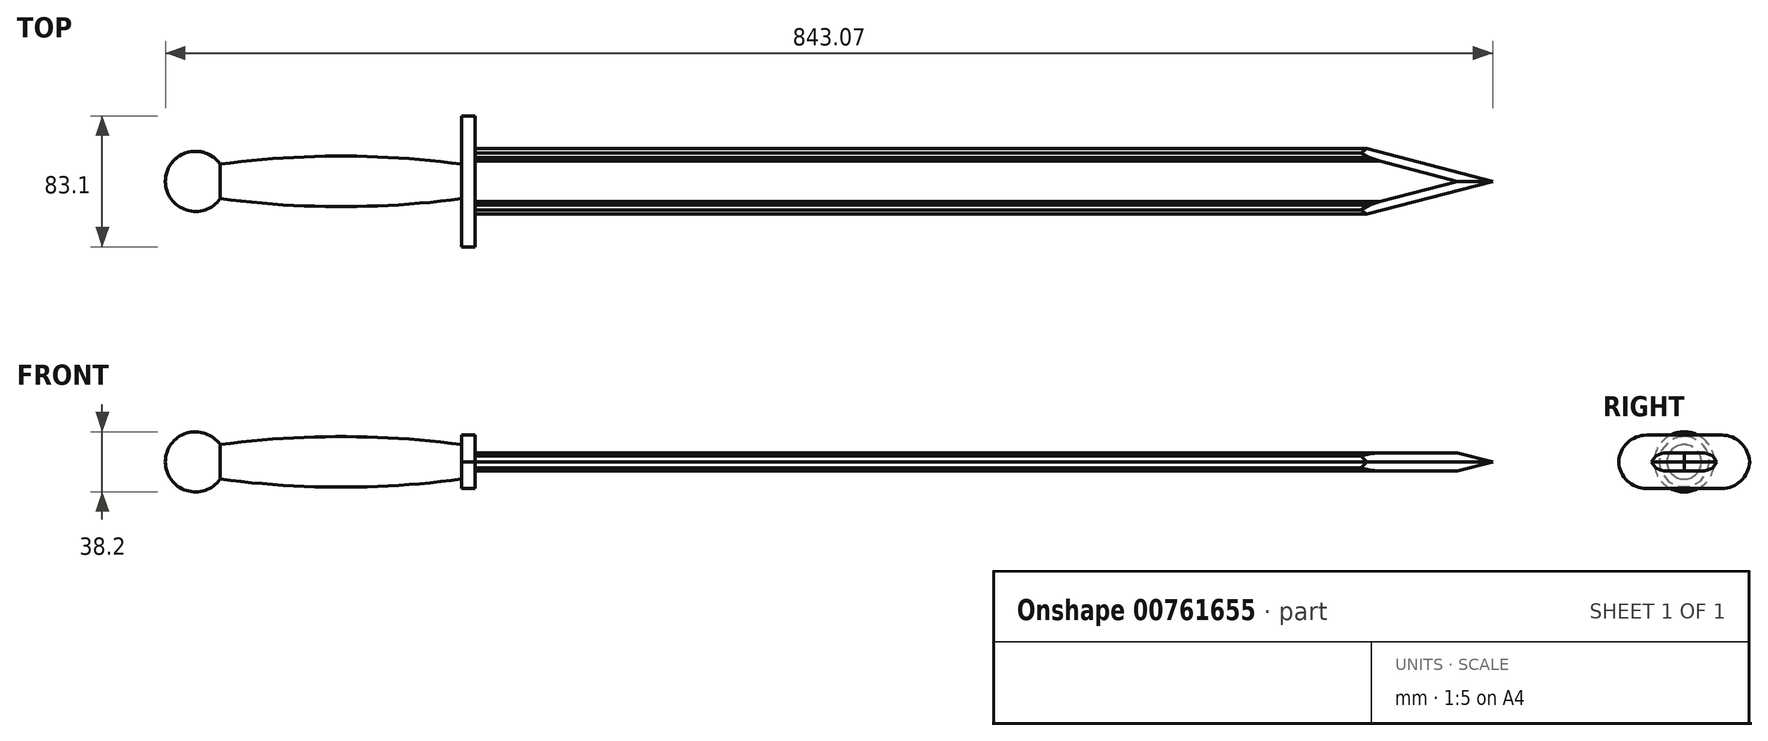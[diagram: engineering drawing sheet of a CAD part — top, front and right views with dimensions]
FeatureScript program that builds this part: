
annotation { "Feature Type Name" : "Feature", "Feature Type Description" : "" }
export const myFeature = defineFeature(function(context is Context, id is Id, definition is map)
    precondition{}
    {
        {
            var Q0;
            Q0=qCreatedBy(makeId("Top.planeOp"),FACE);
            var sketch = newSketch(context, id + "F0", { "sketchPlane" : qUnion([Q0])});
            skLineSegment(sketch, "E0.bottom", {"start": v(-110.92, 0) * mm, "end": v(77.19, 0) * mm});
            skLineSegment(sketch, "E0.right", {"start": v(77.19, 0) * mm, "end": v(77.19, 10.97) * mm});
            skArc(sketch, "E1", {"start": v(-76.16, 10.93) * mm, "mid": v(-97.55, 18.22) * mm, "end": v(-110.92, 0) * mm});
            skArc(sketch, "E2", {"start": v(77.19, 10.97) * mm, "mid": v(0.51, 16.04) * mm, "end": v(-76.16, 10.93) * mm});
            skSolve(sketch);
        }
        {
            var Q0;
            Q0 = qSketchRegion(id + "F0", true);
            var Q1;
            Q1=sQuery(id+"F0.wireOp",EDGE,"E0.bottom");
            revolve(context, id + "F1", {"surfaceOperationType" : NewSurfaceOperationType.NEW, "entities" : qUnion([Q0]), "axis" : qUnion([Q1]), "revolveType" : RevolveType.FULL});
        }
        {
            var Q0;
            Q0=makeQuery(id+"F1.opRevolve","SWEPT_FACE",FACE,{"disambiguationData":[OSD([sQuery(id+"F0.wireOp",EDGE,"E0.right")])]});
            var sketch = newSketch(context, id + "F2", { "sketchPlane" : qUnion([Q0])});
            skLineSegment(sketch, "E3.bottom", {"start": v(-41.57, 17) * mm, "end": v(41.57, 17) * mm});
            skLineSegment(sketch, "E3.top", {"start": v(-41.57, -17) * mm, "end": v(41.57, -17) * mm});
            skLineSegment(sketch, "E3.left", {"start": v(-41.57, 17) * mm, "end": v(-41.57, -17) * mm});
            skLineSegment(sketch, "E3.right", {"start": v(41.57, 17) * mm, "end": v(41.57, -17) * mm});
            skPoint(sketch, "E3.middle", {"position": v(0, 0) * mm});
            skSolve(sketch);
        }
        {
            var Q0;
            Q0 = qSketchRegion(id + "F2", true);
            extrude(context, id + "F3", {"entities" : qUnion([Q0]), "operationType" : NewBodyOperationType.ADD, "depth" : 8.64 * mm, "offsetDistance" : 25.4 * mm});
        }
        {
            var Q0;
            Q0=makeQuery(id+"F3.opExtrude","SWEPT_EDGE",EDGE,{"disambiguationData":[OSD([sQuery(id+"F2.wireOp",EDGE,"E3.bottom"),sQuery(id+"F2.wireOp",EDGE,"E3.right")])]});
            var Q1;
            Q1=makeQuery(id+"F3.opExtrude","SWEPT_EDGE",EDGE,{"disambiguationData":[OSD([sQuery(id+"F2.wireOp",EDGE,"E3.bottom"),sQuery(id+"F2.wireOp",EDGE,"E3.left")])]});
            var Q2;
            Q2=makeQuery(id+"F3.opExtrude","SWEPT_EDGE",EDGE,{"disambiguationData":[OSD([sQuery(id+"F2.wireOp",EDGE,"E3.top"),sQuery(id+"F2.wireOp",EDGE,"E3.left")])]});
            var Q3;
            Q3=makeQuery(id+"F3.opExtrude","SWEPT_EDGE",EDGE,{"disambiguationData":[OSD([sQuery(id+"F2.wireOp",EDGE,"E3.top"),sQuery(id+"F2.wireOp",EDGE,"E3.right")])]});
            fillet(context, id + "F4", {"entities" : qUnion([Q0, Q1, Q2, Q3]), "radius" : 17.78 * mm, "tangentPropagation" : true, "allowEdgeOverflow" : false});
        }
        {
            var Q0;
            Q0=makeQuery(id+"F3.opExtrude","CAP_FACE",FACE,{"disambiguationData":[OSD([sQuery(id+"F2.wireOp",EDGE,"E3.bottom"),sQuery(id+"F2.wireOp",EDGE,"E3.top"),sQuery(id+"F2.wireOp",EDGE,"E3.left"),sQuery(id+"F2.wireOp",EDGE,"E3.right")])],"isStart":false});
            var sketch = newSketch(context, id + "F5", { "sketchPlane" : qUnion([Q0])});
            skLineSegment(sketch, "E4.bottom", {"start": v(22.3, 5.66) * mm, "end": v(-22.3, 5.66) * mm});
            skLineSegment(sketch, "E4.top", {"start": v(22.3, -5.66) * mm, "end": v(-22.3, -5.66) * mm});
            skLineSegment(sketch, "E4.left", {"start": v(22.3, 5.66) * mm, "end": v(22.3, -5.66) * mm});
            skLineSegment(sketch, "E4.right", {"start": v(-22.3, 5.66) * mm, "end": v(-22.3, -5.66) * mm});
            skPoint(sketch, "E4.middle", {"position": v(0, 0) * mm});
            skSolve(sketch);
        }
        {
            var Q0;
            Q0=makeQuery(id+"F5.imprint","IMPRINT",FACE,{"disambiguationData":[TD([[makeQuery(id+"F5.imprint","IMPRINT",EDGE,{"derivedFrom":sQuery(id+"F5.wireOp",EDGE,"E4.bottom")}),1.0]])]});
            extrude(context, id + "F6", {"entities" : qUnion([Q0]), "depth" : 14.48 * mm, "offsetDistance" : 25.4 * mm});
        }
        {
            var Q0;
            Q0=makeQuery(id+"F6.opExtrude","SWEPT_FACE",FACE,{"disambiguationData":[OSD([sQuery(id+"F5.wireOp",EDGE,"E4.bottom")])]});
            var sketch = newSketch(context, id + "F7", { "sketchPlane" : qUnion([Q0])});
            skLineSegment(sketch, "E5.bottom", {"start": v(85.82, 22.3) * mm, "end": v(646.83, 22.3) * mm});
            skLineSegment(sketch, "E5.top", {"start": v(85.82, -22.3) * mm, "end": v(646.83, -22.3) * mm});
            skLineSegment(sketch, "E5.left", {"start": v(85.82, 22.3) * mm, "end": v(85.82, -22.3) * mm});
            skLineSegment(sketch, "E6", {"start": v(732.15, 0) * mm, "end": v(646.83, -22.3) * mm});
            skLineSegment(sketch, "E7", {"start": v(732.15, 0) * mm, "end": v(646.83, 22.3) * mm});
            skSolve(sketch);
        }
        {
            var Q0;
            {var subQ3=sQuery(id+"F7.wireOp",EDGE,"E6");Q0=makeQuery(id+"F7.imprint","IMPRINT",FACE,{"disambiguationData":[TD([[makeQuery(id+"F7.imprint","IMPRINT",EDGE,{"derivedFrom":subQ3}),-1.0]])]});}
            extrude(context, id + "F8", {"entities" : qUnion([Q0]), "oppositeDirection" : true, "depth" : 11.43 * mm, "offsetDistance" : 25.4 * mm});
        }
        {
            var Q0;
            Q0=makeQuery(id+"F8.opExtrude","CAP_EDGE",EDGE,{"disambiguationData":[OSD([sQuery(id+"F7.wireOp",EDGE,"E5.bottom")])],"isStart":true});
            var Q1;
            Q1=makeQuery(id+"F8.opExtrude","CAP_EDGE",EDGE,{"disambiguationData":[OSD([sQuery(id+"F7.wireOp",EDGE,"E5.top")])],"isStart":true});
            var Q2;
            Q2=makeQuery(id+"F8.opExtrude","CAP_EDGE",EDGE,{"disambiguationData":[OSD([sQuery(id+"F7.wireOp",EDGE,"E5.top")])],"isStart":false});
            var Q3;
            Q3=makeQuery(id+"F8.opExtrude","CAP_EDGE",EDGE,{"disambiguationData":[OSD([sQuery(id+"F7.wireOp",EDGE,"E5.bottom")])],"isStart":false});
            chamfer(context, id + "F9", {"entities" : qUnion([Q0, Q1, Q2, Q3]), "chamferType" : ChamferType.TWO_OFFSETS, "width1" : 7.62 * mm, "oppositeDirection" : false, "width2" : 5.7 * mm, "tangentPropagation" : true});
        }
        {
            var Q0;
            {var subQ0=sQuery(id+"F7.wireOp",EDGE,"E5.bottom");var subQ1=sQuery(id+"F5.wireOp",EDGE,"E4.bottom");Q0=makeQuery(id+"F9.opChamfer","BLEND_EDGE",EDGE,{"blendedFrom":[makeQuery(id+"F8.boolean.opBoolean","MERGE",EDGE,{"derivedFrom":[makeQuery(id+"F6.opExtrude","SWEPT_EDGE",EDGE,{"disambiguationData":[OSD([subQ1,sQuery(id+"F5.wireOp",EDGE,"E4.left")])]}),makeQuery(id+"F8.opExtrude","CAP_EDGE",EDGE,{"disambiguationData":[OSD([subQ0])],"isStart":true})]}),makeQuery(id+"F8.boolean.opBoolean","MERGE",FACE,{"derivedFrom":[makeQuery(id+"F6.opExtrude","SWEPT_FACE",FACE,{"disambiguationData":[OSD([subQ1])]}),makeQuery(id+"F8.opExtrude","CAP_FACE",FACE,{"disambiguationData":[OSD([subQ1,subQ0,sQuery(id+"F7.wireOp",EDGE,"E5.top"),sQuery(id+"F7.wireOp",EDGE,"E6"),sQuery(id+"F7.wireOp",EDGE,"E7")])],"isStart":true})]})],"blendedInto":[makeQuery(id+"F8.boolean.opBoolean","MERGE",FACE,{"derivedFrom":[makeQuery(id+"F6.opExtrude","SWEPT_FACE",FACE,{"disambiguationData":[OSD([subQ1])]}),makeQuery(id+"F8.opExtrude","CAP_FACE",FACE,{"disambiguationData":[OSD([subQ1,subQ0,sQuery(id+"F7.wireOp",EDGE,"E5.top"),sQuery(id+"F7.wireOp",EDGE,"E6"),sQuery(id+"F7.wireOp",EDGE,"E7")])],"isStart":true})]})]});}
            var Q1;
            {var subQ0=sQuery(id+"F7.wireOp",EDGE,"E5.top");var subQ1=sQuery(id+"F5.wireOp",EDGE,"E4.bottom");Q1=makeQuery(id+"F9.opChamfer","BLEND_EDGE",EDGE,{"blendedFrom":[makeQuery(id+"F8.boolean.opBoolean","MERGE",EDGE,{"derivedFrom":[makeQuery(id+"F6.opExtrude","SWEPT_EDGE",EDGE,{"disambiguationData":[OSD([subQ1,sQuery(id+"F5.wireOp",EDGE,"E4.right")])]}),makeQuery(id+"F8.opExtrude","CAP_EDGE",EDGE,{"disambiguationData":[OSD([subQ0])],"isStart":true})]}),makeQuery(id+"F8.boolean.opBoolean","MERGE",FACE,{"derivedFrom":[makeQuery(id+"F6.opExtrude","SWEPT_FACE",FACE,{"disambiguationData":[OSD([subQ1])]}),makeQuery(id+"F8.opExtrude","CAP_FACE",FACE,{"disambiguationData":[OSD([subQ1,sQuery(id+"F7.wireOp",EDGE,"E5.bottom"),subQ0,sQuery(id+"F7.wireOp",EDGE,"E6"),sQuery(id+"F7.wireOp",EDGE,"E7")])],"isStart":true})]})],"blendedInto":[makeQuery(id+"F8.boolean.opBoolean","MERGE",FACE,{"derivedFrom":[makeQuery(id+"F6.opExtrude","SWEPT_FACE",FACE,{"disambiguationData":[OSD([subQ1])]}),makeQuery(id+"F8.opExtrude","CAP_FACE",FACE,{"disambiguationData":[OSD([subQ1,sQuery(id+"F7.wireOp",EDGE,"E5.bottom"),subQ0,sQuery(id+"F7.wireOp",EDGE,"E6"),sQuery(id+"F7.wireOp",EDGE,"E7")])],"isStart":true})]})]});}
            chamfer(context, id + "F10", {"entities" : qUnion([Q0, Q1]), "width" : 5.08 * mm, "tangentPropagation" : true});
        }
        {
            var Q0;
            {var subQ0=sQuery(id+"F7.wireOp",EDGE,"E5.bottom");var subQ1=sQuery(id+"F5.wireOp",EDGE,"E4.bottom");var subQ2=makeQuery(id+"F8.boolean.opBoolean","MERGE",FACE,{"derivedFrom":[makeQuery(id+"F6.opExtrude","SWEPT_FACE",FACE,{"disambiguationData":[OSD([subQ1])]}),makeQuery(id+"F8.opExtrude","CAP_FACE",FACE,{"disambiguationData":[OSD([subQ1,subQ0,sQuery(id+"F7.wireOp",EDGE,"E5.top"),sQuery(id+"F7.wireOp",EDGE,"E6"),sQuery(id+"F7.wireOp",EDGE,"E7")])],"isStart":true})]});Q0=makeQuery(id+"F10.opChamfer","BLEND_EDGE",EDGE,{"blendedFrom":[makeQuery(id+"F9.opChamfer","BLEND_EDGE",EDGE,{"blendedFrom":[makeQuery(id+"F8.boolean.opBoolean","MERGE",EDGE,{"derivedFrom":[makeQuery(id+"F6.opExtrude","SWEPT_EDGE",EDGE,{"disambiguationData":[OSD([subQ1,sQuery(id+"F5.wireOp",EDGE,"E4.left")])]}),makeQuery(id+"F8.opExtrude","CAP_EDGE",EDGE,{"disambiguationData":[OSD([subQ0])],"isStart":true})]}),subQ2],"blendedInto":[subQ2]}),subQ2],"blendedInto":[subQ2]});}
            var Q1;
            {var subQ0=sQuery(id+"F7.wireOp",EDGE,"E5.top");var subQ1=sQuery(id+"F5.wireOp",EDGE,"E4.bottom");var subQ2=makeQuery(id+"F8.boolean.opBoolean","MERGE",FACE,{"derivedFrom":[makeQuery(id+"F6.opExtrude","SWEPT_FACE",FACE,{"disambiguationData":[OSD([subQ1])]}),makeQuery(id+"F8.opExtrude","CAP_FACE",FACE,{"disambiguationData":[OSD([subQ1,sQuery(id+"F7.wireOp",EDGE,"E5.bottom"),subQ0,sQuery(id+"F7.wireOp",EDGE,"E6"),sQuery(id+"F7.wireOp",EDGE,"E7")])],"isStart":true})]});Q1=makeQuery(id+"F10.opChamfer","BLEND_EDGE",EDGE,{"blendedFrom":[makeQuery(id+"F9.opChamfer","BLEND_EDGE",EDGE,{"blendedFrom":[makeQuery(id+"F8.boolean.opBoolean","MERGE",EDGE,{"derivedFrom":[makeQuery(id+"F6.opExtrude","SWEPT_EDGE",EDGE,{"disambiguationData":[OSD([subQ1,sQuery(id+"F5.wireOp",EDGE,"E4.right")])]}),makeQuery(id+"F8.opExtrude","CAP_EDGE",EDGE,{"disambiguationData":[OSD([subQ0])],"isStart":true})]}),subQ2],"blendedInto":[subQ2]}),subQ2],"blendedInto":[subQ2]});}
            chamfer(context, id + "F11", {"entities" : qUnion([Q0, Q1]), "width" : 5.08 * mm, "tangentPropagation" : true});
        }
        {
            var Q0;
            Q0=makeQuery(id+"F8.opExtrude","CAP_EDGE",EDGE,{"disambiguationData":[OSD([sQuery(id+"F7.wireOp",EDGE,"E7")])],"isStart":true});
            var Q1;
            Q1=makeQuery(id+"F8.opExtrude","CAP_EDGE",EDGE,{"disambiguationData":[OSD([sQuery(id+"F7.wireOp",EDGE,"E6")])],"isStart":true});
            chamfer(context, id + "F12", {"entities" : qUnion([Q0, Q1]), "width" : 5.7 * mm, "tangentPropagation" : true});
        }
        {
            var Q0;
            {var subQ0=sQuery(id+"F7.wireOp",EDGE,"E5.bottom");Q0=makeQuery(id+"F9.opChamfer","BLEND_EDGE",EDGE,{"blendedFrom":[makeQuery(id+"F8.opExtrude","CAP_EDGE",EDGE,{"disambiguationData":[OSD([subQ0])],"isStart":false}),makeQuery(id+"F8.opExtrude","CAP_FACE",FACE,{"disambiguationData":[OSD([sQuery(id+"F5.wireOp",EDGE,"E4.bottom"),subQ0,sQuery(id+"F7.wireOp",EDGE,"E5.top"),sQuery(id+"F7.wireOp",EDGE,"E6"),sQuery(id+"F7.wireOp",EDGE,"E7")])],"isStart":false})],"blendedInto":[makeQuery(id+"F8.opExtrude","CAP_FACE",FACE,{"disambiguationData":[OSD([sQuery(id+"F5.wireOp",EDGE,"E4.bottom"),subQ0,sQuery(id+"F7.wireOp",EDGE,"E5.top"),sQuery(id+"F7.wireOp",EDGE,"E6"),sQuery(id+"F7.wireOp",EDGE,"E7")])],"isStart":false})]});}
            var Q1;
            {var subQ0=sQuery(id+"F7.wireOp",EDGE,"E5.top");Q1=makeQuery(id+"F9.opChamfer","BLEND_EDGE",EDGE,{"blendedFrom":[makeQuery(id+"F8.opExtrude","CAP_EDGE",EDGE,{"disambiguationData":[OSD([subQ0])],"isStart":false}),makeQuery(id+"F8.opExtrude","CAP_FACE",FACE,{"disambiguationData":[OSD([sQuery(id+"F5.wireOp",EDGE,"E4.bottom"),sQuery(id+"F7.wireOp",EDGE,"E5.bottom"),subQ0,sQuery(id+"F7.wireOp",EDGE,"E6"),sQuery(id+"F7.wireOp",EDGE,"E7")])],"isStart":false})],"blendedInto":[makeQuery(id+"F8.opExtrude","CAP_FACE",FACE,{"disambiguationData":[OSD([sQuery(id+"F5.wireOp",EDGE,"E4.bottom"),sQuery(id+"F7.wireOp",EDGE,"E5.bottom"),subQ0,sQuery(id+"F7.wireOp",EDGE,"E6"),sQuery(id+"F7.wireOp",EDGE,"E7")])],"isStart":false})]});}
            chamfer(context, id + "F13", {"entities" : qUnion([Q0, Q1]), "width" : 5.08 * mm, "tangentPropagation" : true});
        }
        {
            var Q0;
            {var subQ0=sQuery(id+"F7.wireOp",EDGE,"E5.bottom");var subQ1=makeQuery(id+"F8.opExtrude","CAP_FACE",FACE,{"disambiguationData":[OSD([sQuery(id+"F5.wireOp",EDGE,"E4.bottom"),subQ0,sQuery(id+"F7.wireOp",EDGE,"E5.top"),sQuery(id+"F7.wireOp",EDGE,"E6"),sQuery(id+"F7.wireOp",EDGE,"E7")])],"isStart":false});Q0=makeQuery(id+"F13.opChamfer","BLEND_EDGE",EDGE,{"blendedFrom":[makeQuery(id+"F9.opChamfer","BLEND_EDGE",EDGE,{"blendedFrom":[makeQuery(id+"F8.opExtrude","CAP_EDGE",EDGE,{"disambiguationData":[OSD([subQ0])],"isStart":false}),subQ1],"blendedInto":[subQ1]}),subQ1],"blendedInto":[subQ1]});}
            var Q1;
            {var subQ0=sQuery(id+"F7.wireOp",EDGE,"E5.top");var subQ1=makeQuery(id+"F8.opExtrude","CAP_FACE",FACE,{"disambiguationData":[OSD([sQuery(id+"F5.wireOp",EDGE,"E4.bottom"),sQuery(id+"F7.wireOp",EDGE,"E5.bottom"),subQ0,sQuery(id+"F7.wireOp",EDGE,"E6"),sQuery(id+"F7.wireOp",EDGE,"E7")])],"isStart":false});Q1=makeQuery(id+"F13.opChamfer","BLEND_EDGE",EDGE,{"blendedFrom":[makeQuery(id+"F9.opChamfer","BLEND_EDGE",EDGE,{"blendedFrom":[makeQuery(id+"F8.opExtrude","CAP_EDGE",EDGE,{"disambiguationData":[OSD([subQ0])],"isStart":false}),subQ1],"blendedInto":[subQ1]}),subQ1],"blendedInto":[subQ1]});}
            chamfer(context, id + "F14", {"entities" : qUnion([Q0, Q1]), "width" : 5.08 * mm, "tangentPropagation" : true});
        }
        {
            var Q0;
            Q0=makeQuery(id+"F8.opExtrude","CAP_EDGE",EDGE,{"disambiguationData":[OSD([sQuery(id+"F7.wireOp",EDGE,"E7")])],"isStart":false});
            var Q1;
            Q1=makeQuery(id+"F8.opExtrude","CAP_EDGE",EDGE,{"disambiguationData":[OSD([sQuery(id+"F7.wireOp",EDGE,"E6")])],"isStart":false});
            chamfer(context, id + "F15", {"entities" : qUnion([Q0, Q1]), "width" : 5.7 * mm, "tangentPropagation" : true});
        }
        {
            var Q0;
            Q0=makeQuery(id+"F6.opExtrude","SWEPT_EDGE",EDGE,{"disambiguationData":[OSD([sQuery(id+"F5.wireOp",EDGE,"E4.top"),sQuery(id+"F5.wireOp",EDGE,"E4.left")])]});
            var Q1;
            Q1=makeQuery(id+"F6.opExtrude","SWEPT_EDGE",EDGE,{"disambiguationData":[OSD([sQuery(id+"F5.wireOp",EDGE,"E4.top"),sQuery(id+"F5.wireOp",EDGE,"E4.right")])]});
            var Q2;
            Q2=makeQuery(id+"F6.opExtrude","SWEPT_EDGE",EDGE,{"disambiguationData":[OSD([sQuery(id+"F5.wireOp",EDGE,"E4.bottom"),sQuery(id+"F5.wireOp",EDGE,"E4.left")])]});
            var Q3;
            Q3=makeQuery(id+"F6.opExtrude","SWEPT_EDGE",EDGE,{"disambiguationData":[OSD([sQuery(id+"F5.wireOp",EDGE,"E4.bottom"),sQuery(id+"F5.wireOp",EDGE,"E4.right")])]});
            chamfer(context, id + "F16", {"entities" : qUnion([Q0, Q1, Q2, Q3]), "width" : 5.7 * mm, "tangentPropagation" : true});
        }
        {
            var Q0;
            {var subQ0=sQuery(id+"F5.wireOp",EDGE,"E4.bottom");Q0=makeQuery(id+"F16.opChamfer","BLEND_EDGE",EDGE,{"blendedFrom":[makeQuery(id+"F6.opExtrude","SWEPT_EDGE",EDGE,{"disambiguationData":[OSD([subQ0,sQuery(id+"F5.wireOp",EDGE,"E4.left")])]}),makeQuery(id+"F6.opExtrude","SWEPT_FACE",FACE,{"disambiguationData":[OSD([subQ0])]})],"blendedInto":[makeQuery(id+"F6.opExtrude","SWEPT_FACE",FACE,{"disambiguationData":[OSD([subQ0])]})]});}
            var Q1;
            {var subQ0=sQuery(id+"F5.wireOp",EDGE,"E4.bottom");Q1=makeQuery(id+"F16.opChamfer","BLEND_EDGE",EDGE,{"blendedFrom":[makeQuery(id+"F6.opExtrude","SWEPT_EDGE",EDGE,{"disambiguationData":[OSD([subQ0,sQuery(id+"F5.wireOp",EDGE,"E4.right")])]}),makeQuery(id+"F6.opExtrude","SWEPT_FACE",FACE,{"disambiguationData":[OSD([subQ0])]})],"blendedInto":[makeQuery(id+"F6.opExtrude","SWEPT_FACE",FACE,{"disambiguationData":[OSD([subQ0])]})]});}
            chamfer(context, id + "F17", {"entities" : qUnion([Q0, Q1]), "width" : 5.08 * mm, "tangentPropagation" : true});
        }
        {
            var Q0;
            {var subQ0=sQuery(id+"F5.wireOp",EDGE,"E4.bottom");var subQ1=makeQuery(id+"F6.opExtrude","SWEPT_FACE",FACE,{"disambiguationData":[OSD([subQ0])]});Q0=makeQuery(id+"F17.opChamfer","BLEND_EDGE",EDGE,{"blendedFrom":[makeQuery(id+"F16.opChamfer","BLEND_EDGE",EDGE,{"blendedFrom":[makeQuery(id+"F6.opExtrude","SWEPT_EDGE",EDGE,{"disambiguationData":[OSD([subQ0,sQuery(id+"F5.wireOp",EDGE,"E4.left")])]}),subQ1],"blendedInto":[subQ1]}),subQ1],"blendedInto":[subQ1]});}
            var Q1;
            {var subQ0=sQuery(id+"F5.wireOp",EDGE,"E4.bottom");var subQ1=makeQuery(id+"F6.opExtrude","SWEPT_FACE",FACE,{"disambiguationData":[OSD([subQ0])]});Q1=makeQuery(id+"F17.opChamfer","BLEND_EDGE",EDGE,{"blendedFrom":[makeQuery(id+"F16.opChamfer","BLEND_EDGE",EDGE,{"blendedFrom":[makeQuery(id+"F6.opExtrude","SWEPT_EDGE",EDGE,{"disambiguationData":[OSD([subQ0,sQuery(id+"F5.wireOp",EDGE,"E4.right")])]}),subQ1],"blendedInto":[subQ1]}),subQ1],"blendedInto":[subQ1]});}
            chamfer(context, id + "F18", {"entities" : qUnion([Q0, Q1]), "width" : 5.08 * mm, "tangentPropagation" : true});
        }
        {
            var Q0;
            {var subQ0=sQuery(id+"F5.wireOp",EDGE,"E4.top");Q0=makeQuery(id+"F16.opChamfer","BLEND_EDGE",EDGE,{"blendedFrom":[makeQuery(id+"F6.opExtrude","SWEPT_EDGE",EDGE,{"disambiguationData":[OSD([subQ0,sQuery(id+"F5.wireOp",EDGE,"E4.left")])]}),makeQuery(id+"F6.opExtrude","SWEPT_FACE",FACE,{"disambiguationData":[OSD([subQ0])]})],"blendedInto":[makeQuery(id+"F6.opExtrude","SWEPT_FACE",FACE,{"disambiguationData":[OSD([subQ0])]})]});}
            var Q1;
            {var subQ0=sQuery(id+"F5.wireOp",EDGE,"E4.top");Q1=makeQuery(id+"F16.opChamfer","BLEND_EDGE",EDGE,{"blendedFrom":[makeQuery(id+"F6.opExtrude","SWEPT_EDGE",EDGE,{"disambiguationData":[OSD([subQ0,sQuery(id+"F5.wireOp",EDGE,"E4.right")])]}),makeQuery(id+"F6.opExtrude","SWEPT_FACE",FACE,{"disambiguationData":[OSD([subQ0])]})],"blendedInto":[makeQuery(id+"F6.opExtrude","SWEPT_FACE",FACE,{"disambiguationData":[OSD([subQ0])]})]});}
            chamfer(context, id + "F19", {"entities" : qUnion([Q0, Q1]), "width" : 5.08 * mm, "tangentPropagation" : true});
        }
        {
            var Q0;
            {var subQ0=sQuery(id+"F5.wireOp",EDGE,"E4.top");var subQ1=makeQuery(id+"F6.opExtrude","SWEPT_FACE",FACE,{"disambiguationData":[OSD([subQ0])]});Q0=makeQuery(id+"F19.opChamfer","BLEND_EDGE",EDGE,{"blendedFrom":[makeQuery(id+"F16.opChamfer","BLEND_EDGE",EDGE,{"blendedFrom":[makeQuery(id+"F6.opExtrude","SWEPT_EDGE",EDGE,{"disambiguationData":[OSD([subQ0,sQuery(id+"F5.wireOp",EDGE,"E4.right")])]}),subQ1],"blendedInto":[subQ1]}),subQ1],"blendedInto":[subQ1]});}
            var Q1;
            {var subQ0=sQuery(id+"F5.wireOp",EDGE,"E4.top");var subQ1=makeQuery(id+"F6.opExtrude","SWEPT_FACE",FACE,{"disambiguationData":[OSD([subQ0])]});Q1=makeQuery(id+"F19.opChamfer","BLEND_EDGE",EDGE,{"blendedFrom":[makeQuery(id+"F16.opChamfer","BLEND_EDGE",EDGE,{"blendedFrom":[makeQuery(id+"F6.opExtrude","SWEPT_EDGE",EDGE,{"disambiguationData":[OSD([subQ0,sQuery(id+"F5.wireOp",EDGE,"E4.left")])]}),subQ1],"blendedInto":[subQ1]}),subQ1],"blendedInto":[subQ1]});}
            chamfer(context, id + "F20", {"entities" : qUnion([Q0, Q1]), "width" : 5.08 * mm, "tangentPropagation" : true});
        }
        {
            var Q0;
            Q0=makeQuery(id+"F6.opExtrude","SWEPT_BODY",BODY,{"disambiguationData":[OSD([sQuery(id+"F5.wireOp",EDGE,"E4.bottom"),sQuery(id+"F5.wireOp",EDGE,"E4.top"),sQuery(id+"F5.wireOp",EDGE,"E4.left"),sQuery(id+"F5.wireOp",EDGE,"E4.right")])]});
            deleteBodies(context, id + "F21", {"entities" : qUnion([Q0])});
        }
        {
            var Q0;
            Q0=makeQuery(id+"F8.opExtrude","SWEPT_FACE",FACE,{"disambiguationData":[OSD([sQuery(id+"F5.wireOp",EDGE,"E4.bottom")])]});
            extrude(context, id + "F22", {"entities" : qUnion([Q0]), "operationType" : NewBodyOperationType.ADD, "depth" : 20.32 * mm, "offsetDistance" : 25.4 * mm});
        }
    });
